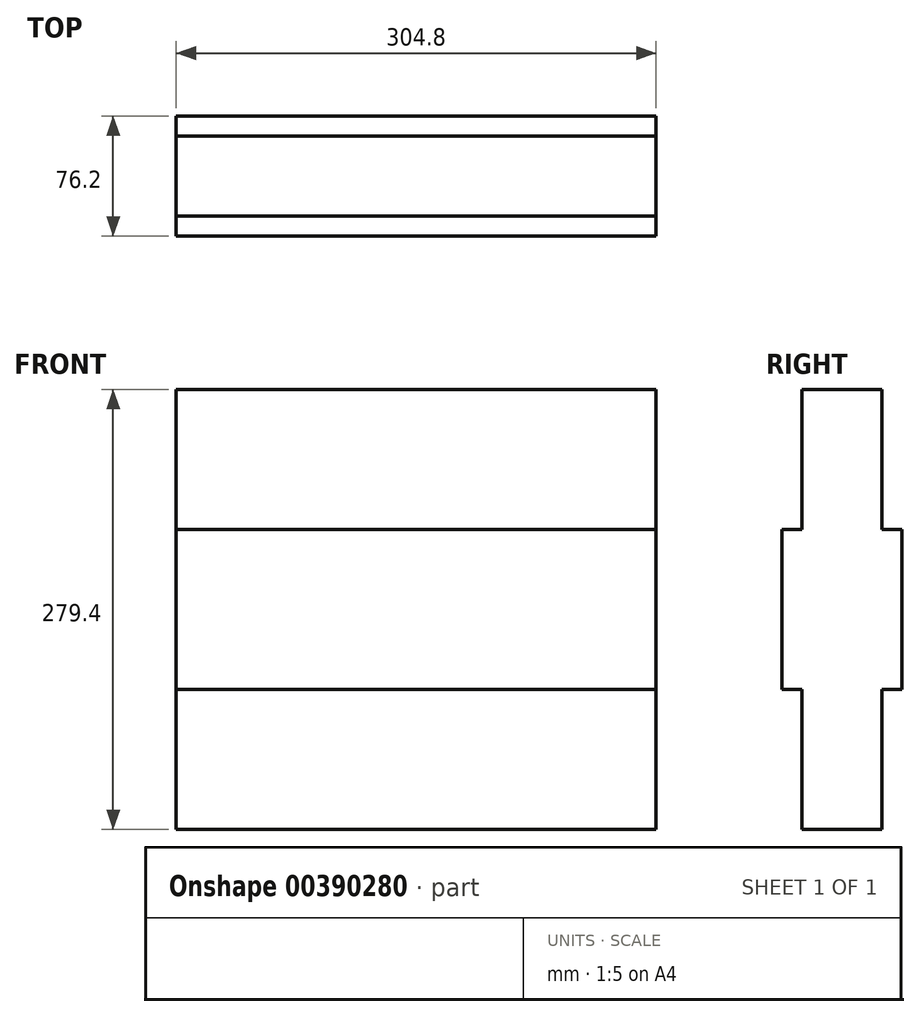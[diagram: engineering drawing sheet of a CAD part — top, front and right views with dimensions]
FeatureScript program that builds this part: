
annotation { "Feature Type Name" : "Feature", "Feature Type Description" : "" }
export const myFeature = defineFeature(function(context is Context, id is Id, definition is map)
    precondition{}
    {
        {
            var Q0;
            Q0=qCreatedBy(makeId("Front.planeOp"),FACE);
            var sketch = newSketch(context, id + "F0", { "sketchPlane" : qUnion([Q0])});
            skLineSegment(sketch, "E0.bottom", {"start": v(-152.4, 139.7) * mm, "end": v(152.4, 139.7) * mm});
            skLineSegment(sketch, "E0.top", {"start": v(-152.4, -139.7) * mm, "end": v(152.4, -139.7) * mm});
            skLineSegment(sketch, "E0.left", {"start": v(-152.4, 139.7) * mm, "end": v(-152.4, -139.7) * mm});
            skLineSegment(sketch, "E0.right", {"start": v(152.4, 139.7) * mm, "end": v(152.4, -139.7) * mm});
            skPoint(sketch, "E0.middle", {"position": v(0, 0) * mm});
            skLineSegment(sketch, "E1", {"start": v(-152.4, -50.8) * mm, "end": v(152.4, -50.8) * mm});
            skLineSegment(sketch, "E2", {"start": v(-152.4, 50.8) * mm, "end": v(152.4, 50.8) * mm});
            skSolve(sketch);
        }
        {
            var Q0;
            {var subQ0=sQuery(id+"F0.wireOp",EDGE,"E1");Q0=makeQuery(id+"F0.imprint","IMPRINT",FACE,{"disambiguationData":[TD([[makeQuery(id+"F0.imprint","IMPRINT",EDGE,{"derivedFrom":subQ0}),1.0]])]});}
            extrude(context, id + "F1", {"entities" : qUnion([Q0]), "endBound" : BoundingType.SYMMETRIC, "depth" : 76.2 * mm});
        }
        {
            var Q0;
            {var subQ0=sQuery(id+"F0.wireOp",EDGE,"E0.bottom");Q0=makeQuery(id+"F0.imprint","IMPRINT",FACE,{"disambiguationData":[TD([[makeQuery(id+"F0.imprint","IMPRINT",EDGE,{"derivedFrom":subQ0}),-1.0]])]});}
            var Q1;
            {var subQ0=sQuery(id+"F0.wireOp",EDGE,"E0.top");Q1=makeQuery(id+"F0.imprint","IMPRINT",FACE,{"disambiguationData":[TD([[makeQuery(id+"F0.imprint","IMPRINT",EDGE,{"derivedFrom":subQ0}),1.0]])]});}
            extrude(context, id + "F2", {"entities" : qUnion([Q0, Q1]), "operationType" : NewBodyOperationType.ADD, "endBound" : BoundingType.SYMMETRIC, "depth" : 50.8 * mm});
        }
    });
